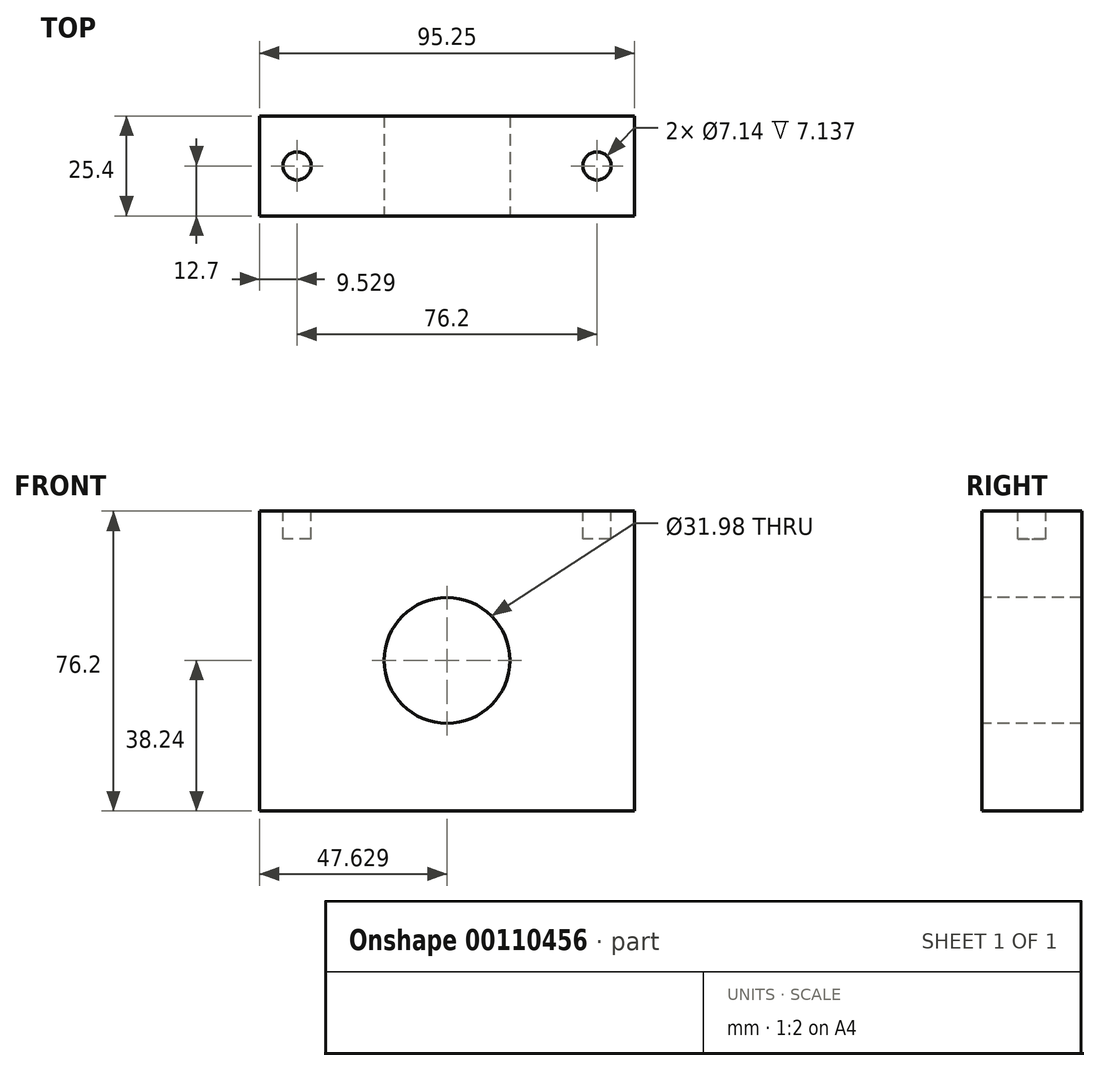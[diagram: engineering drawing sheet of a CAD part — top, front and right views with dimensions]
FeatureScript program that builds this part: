
annotation { "Feature Type Name" : "Feature", "Feature Type Description" : "" }
export const myFeature = defineFeature(function(context is Context, id is Id, definition is map)
    precondition{}
    {
        {
            var Q0;
            Q0=qCreatedBy(makeId("Front.planeOp"),FACE);
            var sketch = newSketch(context, id + "F0", { "sketchPlane" : qUnion([Q0])});
            skLineSegment(sketch, "E0", {"start": v(-40.7, 37.96) * mm, "end": v(54.54, 37.96) * mm});
            skLineSegment(sketch, "E1", {"start": v(54.54, 37.96) * mm, "end": v(54.54, -38.24) * mm});
            skLineSegment(sketch, "E2", {"start": v(-40.7, 37.96) * mm, "end": v(-40.7, -38.24) * mm});
            skLineSegment(sketch, "E3", {"start": v(-40.7, -38.24) * mm, "end": v(54.54, -38.24) * mm});
            skSolve(sketch);
        }
        {
            var Q0;
            Q0=makeQuery(id+"F0.imprint","IMPRINT",FACE,{"disambiguationData":[TD([[makeQuery(id+"F0.imprint","IMPRINT",EDGE,{"derivedFrom":sQuery(id+"F0.wireOp",EDGE,"E0")}),-1.0]])]});
            extrude(context, id + "F1", {"entities" : qUnion([Q0]), "depth" : 25.4 * mm});
        }
        {
            var Q0;
            Q0=makeQuery(id+"F1.opExtrude","CAP_FACE",FACE,{"disambiguationData":[OSD([sQuery(id+"F0.wireOp",EDGE,"E0"),sQuery(id+"F0.wireOp",EDGE,"E1"),sQuery(id+"F0.wireOp",EDGE,"E2"),sQuery(id+"F0.wireOp",EDGE,"E3")])],"isStart":false});
            var sketch = newSketch(context, id + "F2", { "sketchPlane" : qUnion([Q0])});
            skCircle(sketch, "E4", {"center": v(6.92, 0) * mm, "radius": 16 * mm});
            skPoint(sketch, "E4.centerSnap0", {"position": v(6.92, 37.96) * mm});
            skSolve(sketch);
        }
        {
            var Q0;
            Q0=makeQuery(id+"F2.imprint","IMPRINT",FACE,{"disambiguationData":[TD([[makeQuery(id+"F2.imprint","IMPRINT",EDGE,{"derivedFrom":sQuery(id+"F2.wireOp",EDGE,"E4")}),1.0]])]});
            extrude(context, id + "F3", {"entities" : qUnion([Q0]), "operationType" : NewBodyOperationType.REMOVE, "oppositeDirection" : true, "depth" : 47.5 * mm});
        }
        {
            var Q0;
            Q0=makeQuery(id+"F1.opExtrude","SWEPT_FACE",FACE,{"disambiguationData":[OSD([sQuery(id+"F0.wireOp",EDGE,"E0")])]});
            var sketch = newSketch(context, id + "F4", { "sketchPlane" : qUnion([Q0])});
            skLineSegment(sketch, "E5", {"start": v(54.54, -12.7) * mm, "end": v(45.02, -12.7) * mm, "construction": true});
            skPoint(sketch, "E5.endSnap0", {"position": v(54.54, -12.7) * mm});
            skCircle(sketch, "E6", {"center": v(45.02, -12.7) * mm, "radius": 3.57 * mm});
            skLineSegment(sketch, "E7", {"start": v(45.02, -12.7) * mm, "end": v(-31.18, -12.7) * mm});
            skPoint(sketch, "E7.endSnap0", {"position": v(-40.7, -12.7) * mm});
            skCircle(sketch, "E8", {"center": v(-31.18, -12.7) * mm, "radius": 3.57 * mm});
            skSolve(sketch);
        }
        {
            var Q0;
            Q0=makeQuery(id+"F4.imprint","IMPRINT",FACE,{"disambiguationData":[TD([[makeQuery(id+"F4.imprint","IMPRINT",EDGE,{"derivedFrom":sQuery(id+"F4.wireOp",EDGE,"E8")}),1.0]])]});
            var Q1;
            Q1=makeQuery(id+"F4.imprint","IMPRINT",FACE,{"disambiguationData":[TD([[makeQuery(id+"F4.imprint","IMPRINT",EDGE,{"derivedFrom":sQuery(id+"F4.wireOp",EDGE,"E6")}),1.0]])]});
            extrude(context, id + "F5", {"entities" : qUnion([Q0, Q1]), "operationType" : NewBodyOperationType.REMOVE, "oppositeDirection" : true, "depth" : 7.14 * mm});
        }
    });
